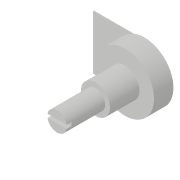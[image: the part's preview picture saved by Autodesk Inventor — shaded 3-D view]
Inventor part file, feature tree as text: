
AUTODESK INVENTOR PART (.ipt)
format: ipt  version: 2018 (Build 220112000, 112)  size: 117,248 bytes
history: native  units: in
note: dims shown in document units (in); Inventor stores cm internally (conversion verified against a paired STEP export)
features: extrude x5, sketch x5
ambient origin geometry x8: Origin, YZ Plane, XZ Plane, XY Plane, X Axis, Y Axis, Z Axis, Center Point
bodies: Solid1 (feature_tree)
feature tree (10):
  extrude  "Extrusion1"  Depth=0.25in TaperAngle=0.0deg
  extrude  "Extrusion2"  Depth=0.38in TaperAngle=0.0deg
  extrude  "Extrusion3"  Depth=0.495in TaperAngle=0.0deg
  extrude  "Extrusion4"  Depth=0.047in
  extrude  "Extrusion5"  Depth=0.35in
  sketch  "Sketch1"  dims[d0=0.75in d1=0.25in d2=0.0in]
  sketch  "Sketch2"  dims[d3=0.375in d4=0.38in d5=0.0in]
  sketch  "Sketch3"  dims[d6=0.25in d7=0.495in d8=0.0in]
  sketch  "Sketch4"  dims[d9=0.047in d10=0.5in]
  sketch  "Sketch5"  dims[d11=0.25in d12=0.0235in d13=0.063in d14=0.0in d15=0.65in d16=0.01in d17=0.0in d18=0.7in d19=0.35in]
